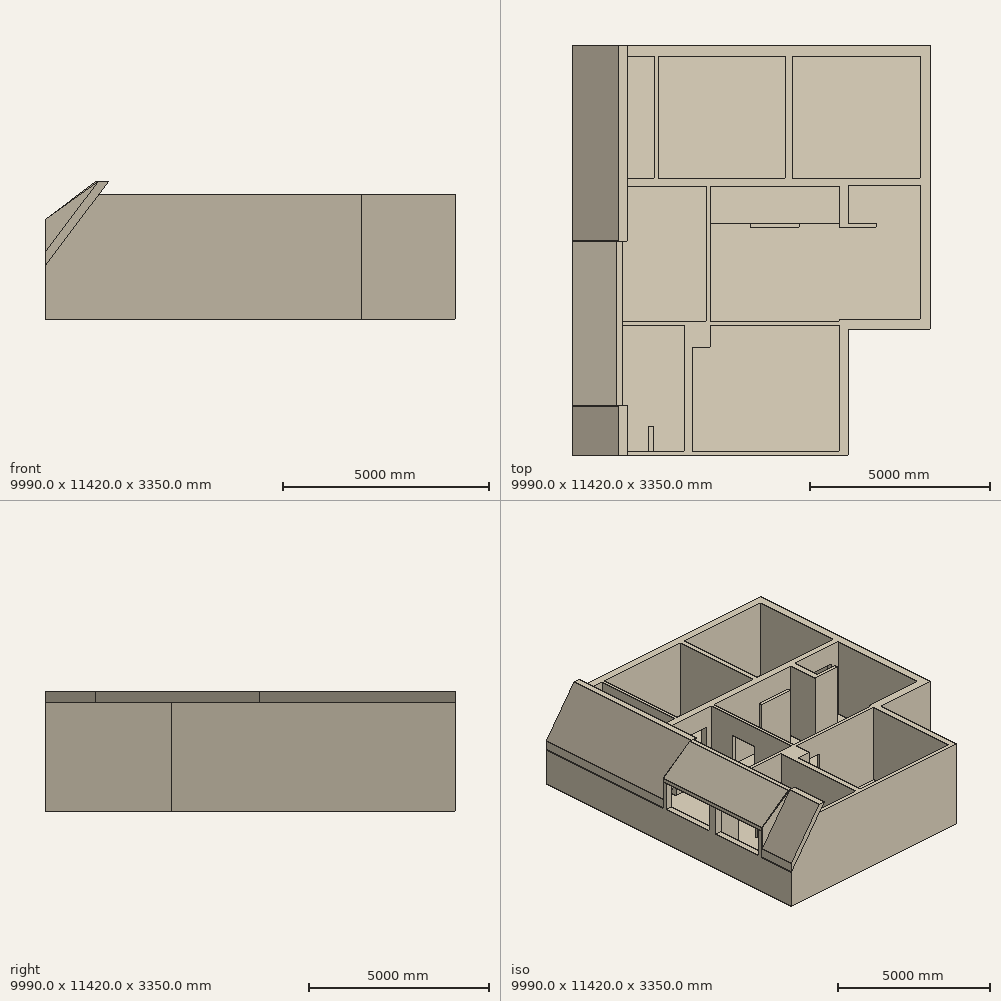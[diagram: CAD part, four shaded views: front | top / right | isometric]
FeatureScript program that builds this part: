
annotation { "Feature Type Name" : "Feature", "Feature Type Description" : "" }
export const myFeature = defineFeature(function(context is Context, id is Id, definition is map)
    precondition{}
    {
        {
            var Q0;
            Q0=qCreatedBy(makeId("Top.planeOp"),FACE);
            var sketch = newSketch(context, id + "F0", { "sketchPlane" : qUnion([Q0])});
            skLineSegment(sketch, "E0", {"start": v(0, 0) * mm, "end": v(0, 11420) * mm});
            skLineSegment(sketch, "E1", {"start": v(0, 11420) * mm, "end": v(9990, 11420) * mm});
            skLineSegment(sketch, "E2", {"start": v(0, 0) * mm, "end": v(7690, 0) * mm});
            skLineSegment(sketch, "E3", {"start": v(7690, 0) * mm, "end": v(7690, 3500) * mm});
            skLineSegment(sketch, "E4", {"start": v(7690, 3500) * mm, "end": v(9990, 3500) * mm});
            skLineSegment(sketch, "E5", {"start": v(9990, 3500) * mm, "end": v(9990, 11420) * mm});
            skSolve(sketch);
        }
        {
            var Q0;
            Q0 = qSketchRegion(id + "F0", true);
            extrude(context, id + "F1", {"entities" : qUnion([Q0]), "depth" : 300 * mm});
        }
        {
            var Q0;
            Q0=makeQuery(id+"F1.opExtrude","CAP_FACE",FACE,{"disambiguationData":[OSD([sQuery(id+"F0.wireOp",EDGE,"E0"),sQuery(id+"F0.wireOp",EDGE,"E1"),sQuery(id+"F0.wireOp",EDGE,"E2"),sQuery(id+"F0.wireOp",EDGE,"E3"),sQuery(id+"F0.wireOp",EDGE,"E4"),sQuery(id+"F0.wireOp",EDGE,"E5")])],"isStart":false});
            var sketch = newSketch(context, id + "F2", { "sketchPlane" : qUnion([Q0])});
            skLineSegment(sketch, "E6.bottom", {"start": v(0, 0) * mm, "end": v(7690, 0) * mm});
            skLineSegment(sketch, "E6.top", {"start": v(0, 120) * mm, "end": v(7690, 120) * mm});
            skLineSegment(sketch, "E6.left", {"start": v(0, 0) * mm, "end": v(0, 120) * mm});
            skLineSegment(sketch, "E6.right", {"start": v(7690, 0) * mm, "end": v(7690, 120) * mm});
            skSolve(sketch);
        }
        {
            var Q0;
            Q0 = qSketchRegion(id + "F2", true);
            extrude(context, id + "F3", {"entities" : qUnion([Q0]), "operationType" : NewBodyOperationType.ADD, "depth" : 2750 * mm});
        }
        {
            var Q0;
            Q0=makeQuery(id+"F1.opExtrude","CAP_FACE",FACE,{"disambiguationData":[OSD([sQuery(id+"F0.wireOp",EDGE,"E0"),sQuery(id+"F0.wireOp",EDGE,"E1"),sQuery(id+"F0.wireOp",EDGE,"E2"),sQuery(id+"F0.wireOp",EDGE,"E3"),sQuery(id+"F0.wireOp",EDGE,"E4"),sQuery(id+"F0.wireOp",EDGE,"E5")])],"isStart":false});
            var sketch = newSketch(context, id + "F4", { "sketchPlane" : qUnion([Q0])});
            skLineSegment(sketch, "E7.bottom", {"start": v(0, 120) * mm, "end": v(240, 120) * mm});
            skLineSegment(sketch, "E7.top", {"start": v(0, 7480) * mm, "end": v(240, 7480) * mm});
            skLineSegment(sketch, "E7.left", {"start": v(0, 120) * mm, "end": v(0, 7480) * mm});
            skLineSegment(sketch, "E7.right", {"start": v(240, 120) * mm, "end": v(240, 7480) * mm});
            skSolve(sketch);
        }
        {
            var Q0;
            Q0 = qSketchRegion(id + "F4", true);
            extrude(context, id + "F5", {"entities" : qUnion([Q0]), "operationType" : NewBodyOperationType.ADD, "depth" : 2750 * mm});
        }
        {
            var Q0;
            Q0=makeQuery(id+"F1.opExtrude","CAP_FACE",FACE,{"disambiguationData":[OSD([sQuery(id+"F0.wireOp",EDGE,"E0"),sQuery(id+"F0.wireOp",EDGE,"E1"),sQuery(id+"F0.wireOp",EDGE,"E2"),sQuery(id+"F0.wireOp",EDGE,"E3"),sQuery(id+"F0.wireOp",EDGE,"E4"),sQuery(id+"F0.wireOp",EDGE,"E5")])],"isStart":false});
            var sketch = newSketch(context, id + "F6", { "sketchPlane" : qUnion([Q0])});
            skLineSegment(sketch, "E8.bottom", {"start": v(7690, 120) * mm, "end": v(7450, 120) * mm});
            skLineSegment(sketch, "E8.left", {"start": v(7690, 120) * mm, "end": v(7690, 7480) * mm});
            skLineSegment(sketch, "E8.right", {"start": v(7450, 120) * mm, "end": v(7450, 7480) * mm});
            skLineSegment(sketch, "E9.bottom", {"start": v(0, 7480) * mm, "end": v(7450, 7480) * mm});
            skLineSegment(sketch, "E9.top", {"start": v(0, 7720) * mm, "end": v(7690, 7720) * mm});
            skLineSegment(sketch, "E9.left", {"start": v(0, 7480) * mm, "end": v(0, 7720) * mm});
            skLineSegment(sketch, "E9.right", {"start": v(7690, 7480) * mm, "end": v(7690, 7720) * mm});
            skSolve(sketch);
        }
        {
            var Q0;
            Q0 = qSketchRegion(id + "F6", true);
            extrude(context, id + "F7", {"entities" : qUnion([Q0]), "operationType" : NewBodyOperationType.ADD, "depth" : 2750 * mm});
        }
        {
            var Q0;
            {var subQ0=sQuery(id+"F0.wireOp",EDGE,"E5");var subQ1=sQuery(id+"F0.wireOp",EDGE,"E0");var subQ2=sQuery(id+"F0.wireOp",EDGE,"E3");var subQ3=sQuery(id+"F0.wireOp",EDGE,"E1");var subQ4=sQuery(id+"F0.wireOp",EDGE,"E4");Q0=makeQuery(id+"F7.boolean.opBoolean","SPLIT",FACE,{"disambiguationData":[TD([makeQuery(id+"F1.opExtrude","SWEPT_FACE",FACE,{"disambiguationData":[OSD([subQ1])]})])],"derivedFrom":makeQuery(id+"F1.opExtrude","CAP_FACE",FACE,{"disambiguationData":[OSD([subQ1,subQ3,sQuery(id+"F0.wireOp",EDGE,"E2"),subQ2,subQ4,subQ0])],"isStart":false})});}
            var sketch = newSketch(context, id + "F8", { "sketchPlane" : qUnion([Q0])});
            skLineSegment(sketch, "E10.top", {"start": v(0, 7720) * mm, "end": v(300, 7720) * mm});
            skLineSegment(sketch, "E10.left", {"start": v(0, 11420) * mm, "end": v(0, 7720) * mm});
            skLineSegment(sketch, "E11.top", {"start": v(9690, 11120) * mm, "end": v(300, 11120) * mm});
            skLineSegment(sketch, "E11.left", {"start": v(9990, 11420) * mm, "end": v(9990, 11120) * mm});
            skLineSegment(sketch, "E12.top", {"start": v(9990, 3500) * mm, "end": v(9690, 3500) * mm});
            skLineSegment(sketch, "E12.left", {"start": v(9990, 11420) * mm, "end": v(9990, 3500) * mm});
            skLineSegment(sketch, "E13", {"start": v(300, 7720) * mm, "end": v(300, 11120) * mm});
            skLineSegment(sketch, "E14", {"start": v(9690, 3800) * mm, "end": v(9690, 11120) * mm});
            skLineSegment(sketch, "E15.top", {"start": v(7690, 3800) * mm, "end": v(9690, 3800) * mm});
            skLineSegment(sketch, "E15.left", {"start": v(7690, 3500) * mm, "end": v(7690, 3800) * mm});
            skLineSegment(sketch, "E16", {"start": v(7690, 3500) * mm, "end": v(9690, 3500) * mm});
            skLineSegment(sketch, "E17", {"start": v(9990, 11420) * mm, "end": v(0, 11420) * mm});
            skSolve(sketch);
        }
        {
            var Q0;
            Q0=makeQuery(id+"F7.boolean.opBoolean","SPLIT",FACE,{"disambiguationData":[TD([makeQuery(id+"F3.opExtrude","SWEPT_FACE",FACE,{"disambiguationData":[OSD([sQuery(id+"F2.wireOp",EDGE,"E6.top")])]})])],"derivedFrom":makeQuery(id+"F1.opExtrude","CAP_FACE",FACE,{"disambiguationData":[OSD([sQuery(id+"F0.wireOp",EDGE,"E0"),sQuery(id+"F0.wireOp",EDGE,"E1"),sQuery(id+"F0.wireOp",EDGE,"E2"),sQuery(id+"F0.wireOp",EDGE,"E3"),sQuery(id+"F0.wireOp",EDGE,"E4"),sQuery(id+"F0.wireOp",EDGE,"E5")])],"isStart":false})});
            var sketch = newSketch(context, id + "F9", { "sketchPlane" : qUnion([Q0])});
            skLineSegment(sketch, "E18.bottom", {"start": v(240, 3730) * mm, "end": v(7450, 3730) * mm});
            skLineSegment(sketch, "E18.top", {"start": v(240, 3620) * mm, "end": v(7450, 3620) * mm});
            skLineSegment(sketch, "E18.left", {"start": v(240, 3730) * mm, "end": v(240, 3620) * mm});
            skLineSegment(sketch, "E18.right", {"start": v(7450, 3730) * mm, "end": v(7450, 3620) * mm});
            skSolve(sketch);
        }
        {
            var Q0;
            Q0 = qSketchRegion(id + "F9", true);
            extrude(context, id + "F10", {"entities" : qUnion([Q0]), "operationType" : NewBodyOperationType.ADD, "depth" : 2750 * mm});
        }
        {
            var Q0;
            Q0 = qSketchRegion(id + "F8", true);
            extrude(context, id + "F11", {"entities" : qUnion([Q0]), "operationType" : NewBodyOperationType.ADD, "depth" : 2750 * mm});
        }
        {
            var Q0;
            {var subQ0=makeQuery(id+"F3.opExtrude","SWEPT_FACE",FACE,{"disambiguationData":[OSD([sQuery(id+"F2.wireOp",EDGE,"E6.top")])]});Q0=makeQuery(id+"F10.boolean.opBoolean","SPLIT",FACE,{"disambiguationData":[TD([subQ0])],"derivedFrom":makeQuery(id+"F7.boolean.opBoolean","SPLIT",FACE,{"disambiguationData":[TD([subQ0])],"derivedFrom":makeQuery(id+"F1.opExtrude","CAP_FACE",FACE,{"disambiguationData":[OSD([sQuery(id+"F0.wireOp",EDGE,"E0"),sQuery(id+"F0.wireOp",EDGE,"E1"),sQuery(id+"F0.wireOp",EDGE,"E2"),sQuery(id+"F0.wireOp",EDGE,"E3"),sQuery(id+"F0.wireOp",EDGE,"E4"),sQuery(id+"F0.wireOp",EDGE,"E5")])],"isStart":false})})});}
            var sketch = newSketch(context, id + "F12", { "sketchPlane" : qUnion([Q0])});
            skLineSegment(sketch, "E19.bottom", {"start": v(3740, 120) * mm, "end": v(3850, 120) * mm});
            skLineSegment(sketch, "E19.top", {"start": v(3740, 3620) * mm, "end": v(3850, 3620) * mm});
            skLineSegment(sketch, "E19.left", {"start": v(3740, 120) * mm, "end": v(3740, 3620) * mm});
            skLineSegment(sketch, "E19.right", {"start": v(3850, 120) * mm, "end": v(3850, 3620) * mm});
            skSolve(sketch);
        }
        {
            var Q0;
            Q0 = qSketchRegion(id + "F12", true);
            extrude(context, id + "F13", {"entities" : qUnion([Q0]), "operationType" : NewBodyOperationType.ADD, "depth" : 2750 * mm});
        }
        {
            var Q0;
            {var subQ2=makeQuery(id+"F7.opExtrude","SWEPT_FACE",FACE,{"disambiguationData":[OSD([sQuery(id+"F6.wireOp",EDGE,"E9.bottom")])]});Q0=makeQuery(id+"F10.boolean.opBoolean","SPLIT",FACE,{"disambiguationData":[TD([subQ2])],"derivedFrom":makeQuery(id+"F7.boolean.opBoolean","SPLIT",FACE,{"disambiguationData":[TD([makeQuery(id+"F3.opExtrude","SWEPT_FACE",FACE,{"disambiguationData":[OSD([sQuery(id+"F2.wireOp",EDGE,"E6.top")])]})])],"derivedFrom":makeQuery(id+"F1.opExtrude","CAP_FACE",FACE,{"disambiguationData":[OSD([sQuery(id+"F0.wireOp",EDGE,"E0"),sQuery(id+"F0.wireOp",EDGE,"E1"),sQuery(id+"F0.wireOp",EDGE,"E2"),sQuery(id+"F0.wireOp",EDGE,"E3"),sQuery(id+"F0.wireOp",EDGE,"E4"),sQuery(id+"F0.wireOp",EDGE,"E5")])],"isStart":false})})});}
            var sketch = newSketch(context, id + "F14", { "sketchPlane" : qUnion([Q0])});
            skLineSegment(sketch, "E20.bottom", {"start": v(3740, 3730) * mm, "end": v(3850, 3730) * mm});
            skLineSegment(sketch, "E20.top", {"start": v(3740, 7480) * mm, "end": v(3850, 7480) * mm});
            skLineSegment(sketch, "E20.left", {"start": v(3740, 3730) * mm, "end": v(3740, 7480) * mm});
            skLineSegment(sketch, "E20.right", {"start": v(3850, 3730) * mm, "end": v(3850, 7480) * mm});
            skSolve(sketch);
        }
        {
            var Q0;
            Q0 = qSketchRegion(id + "F14", true);
            extrude(context, id + "F15", {"entities" : qUnion([Q0]), "operationType" : NewBodyOperationType.ADD, "depth" : 2750 * mm});
        }
        {
            var Q0;
            {var subQ0=sQuery(id+"F0.wireOp",EDGE,"E5");var subQ1=sQuery(id+"F0.wireOp",EDGE,"E0");var subQ2=sQuery(id+"F0.wireOp",EDGE,"E3");var subQ3=sQuery(id+"F0.wireOp",EDGE,"E1");var subQ4=sQuery(id+"F0.wireOp",EDGE,"E4");Q0=makeQuery(id+"F7.boolean.opBoolean","SPLIT",FACE,{"disambiguationData":[TD([makeQuery(id+"F1.opExtrude","SWEPT_FACE",FACE,{"disambiguationData":[OSD([subQ1])]})])],"derivedFrom":makeQuery(id+"F1.opExtrude","CAP_FACE",FACE,{"disambiguationData":[OSD([subQ1,subQ3,sQuery(id+"F0.wireOp",EDGE,"E2"),subQ2,subQ4,subQ0])],"isStart":false})});}
            var sketch = newSketch(context, id + "F16", { "sketchPlane" : qUnion([Q0])});
            skLineSegment(sketch, "E21.bottom", {"start": v(2300, 11120) * mm, "end": v(2410, 11120) * mm});
            skLineSegment(sketch, "E21.top", {"start": v(2300, 7720) * mm, "end": v(2410, 7720) * mm});
            skLineSegment(sketch, "E21.left", {"start": v(2300, 11120) * mm, "end": v(2300, 7720) * mm});
            skLineSegment(sketch, "E21.right", {"start": v(2410, 11120) * mm, "end": v(2410, 7720) * mm});
            skSolve(sketch);
        }
        {
            var Q0;
            Q0 = qSketchRegion(id + "F16", true);
            extrude(context, id + "F17", {"entities" : qUnion([Q0]), "operationType" : NewBodyOperationType.ADD, "depth" : 2750 * mm});
        }
        {
            var Q0;
            {var subQ3=sQuery(id+"F0.wireOp",EDGE,"E3");var subQ4=makeQuery(id+"F1.opExtrude","SWEPT_FACE",FACE,{"disambiguationData":[OSD([subQ3])]});var subQ5=sQuery(id+"F0.wireOp",EDGE,"E5");var subQ6=sQuery(id+"F0.wireOp",EDGE,"E0");var subQ7=sQuery(id+"F0.wireOp",EDGE,"E1");var subQ8=sQuery(id+"F0.wireOp",EDGE,"E4");Q0=makeQuery(id+"F17.boolean.opBoolean","SPLIT",FACE,{"disambiguationData":[TD([subQ4])],"derivedFrom":makeQuery(id+"F7.boolean.opBoolean","SPLIT",FACE,{"disambiguationData":[TD([makeQuery(id+"F1.opExtrude","SWEPT_FACE",FACE,{"disambiguationData":[OSD([subQ6])]})])],"derivedFrom":makeQuery(id+"F1.opExtrude","CAP_FACE",FACE,{"disambiguationData":[OSD([subQ6,subQ7,sQuery(id+"F0.wireOp",EDGE,"E2"),subQ3,subQ8,subQ5])],"isStart":false})})});}
            var sketch = newSketch(context, id + "F18", { "sketchPlane" : qUnion([Q0])});
            skLineSegment(sketch, "E22.bottom", {"start": v(7690, 7720) * mm, "end": v(9690, 7720) * mm});
            skLineSegment(sketch, "E22.top", {"start": v(7690, 7520) * mm, "end": v(9690, 7520) * mm});
            skLineSegment(sketch, "E22.left", {"start": v(7690, 7720) * mm, "end": v(7690, 7520) * mm});
            skLineSegment(sketch, "E22.right", {"start": v(9690, 7720) * mm, "end": v(9690, 7520) * mm});
            skSolve(sketch);
        }
        {
            var Q0;
            Q0 = qSketchRegion(id + "F18", true);
            extrude(context, id + "F19", {"entities" : qUnion([Q0]), "operationType" : NewBodyOperationType.ADD, "depth" : 2750 * mm});
        }
        {
            var Q0;
            {var subQ3=makeQuery(id+"F7.opExtrude","SWEPT_FACE",FACE,{"disambiguationData":[OSD([sQuery(id+"F6.wireOp",EDGE,"E9.top")])]});var subQ6=sQuery(id+"F0.wireOp",EDGE,"E3");var subQ7=makeQuery(id+"F1.opExtrude","SWEPT_FACE",FACE,{"disambiguationData":[OSD([subQ6])]});var subQ8=sQuery(id+"F0.wireOp",EDGE,"E5");var subQ9=sQuery(id+"F0.wireOp",EDGE,"E0");var subQ10=sQuery(id+"F0.wireOp",EDGE,"E1");var subQ11=sQuery(id+"F0.wireOp",EDGE,"E4");Q0=makeQuery(id+"F19.boolean.opBoolean","SPLIT",FACE,{"disambiguationData":[TD([subQ3])],"derivedFrom":makeQuery(id+"F17.boolean.opBoolean","SPLIT",FACE,{"disambiguationData":[TD([subQ7])],"derivedFrom":makeQuery(id+"F7.boolean.opBoolean","SPLIT",FACE,{"disambiguationData":[TD([makeQuery(id+"F1.opExtrude","SWEPT_FACE",FACE,{"disambiguationData":[OSD([subQ9])]})])],"derivedFrom":makeQuery(id+"F1.opExtrude","CAP_FACE",FACE,{"disambiguationData":[OSD([subQ9,subQ10,sQuery(id+"F0.wireOp",EDGE,"E2"),subQ6,subQ11,subQ8])],"isStart":false})})})});}
            var sketch = newSketch(context, id + "F20", { "sketchPlane" : qUnion([Q0])});
            skLineSegment(sketch, "E23.bottom", {"start": v(5950, 11120) * mm, "end": v(6150, 11120) * mm});
            skLineSegment(sketch, "E23.top", {"start": v(5950, 7720) * mm, "end": v(6150, 7720) * mm});
            skLineSegment(sketch, "E23.left", {"start": v(5950, 11120) * mm, "end": v(5950, 7720) * mm});
            skLineSegment(sketch, "E23.right", {"start": v(6150, 11120) * mm, "end": v(6150, 7720) * mm});
            skSolve(sketch);
        }
        {
            var Q0;
            Q0 = qSketchRegion(id + "F20", true);
            extrude(context, id + "F21", {"entities" : qUnion([Q0]), "operationType" : NewBodyOperationType.ADD, "depth" : 2750 * mm});
        }
        {
            var Q0;
            Q0=makeQuery(id+"F21.boolean.opBoolean","MERGE",FACE,{"derivedFrom":[makeQuery(id+"F19.boolean.opBoolean","MERGE",FACE,{"derivedFrom":[makeQuery(id+"F17.boolean.opBoolean","MERGE",FACE,{"derivedFrom":[makeQuery(id+"F15.boolean.opBoolean","MERGE",FACE,{"derivedFrom":[makeQuery(id+"F13.boolean.opBoolean","MERGE",FACE,{"derivedFrom":[makeQuery(id+"F11.boolean.opBoolean","MERGE",FACE,{"derivedFrom":[makeQuery(id+"F10.boolean.opBoolean","MERGE",FACE,{"derivedFrom":[makeQuery(id+"F7.boolean.opBoolean","MERGE",FACE,{"derivedFrom":[makeQuery(id+"F5.boolean.opBoolean","MERGE",FACE,{"derivedFrom":[makeQuery(id+"F3.opExtrude","CAP_FACE",FACE,{"disambiguationData":[OSD([sQuery(id+"F2.wireOp",EDGE,"E6.bottom"),sQuery(id+"F2.wireOp",EDGE,"E6.top"),sQuery(id+"F2.wireOp",EDGE,"E6.left"),sQuery(id+"F2.wireOp",EDGE,"E6.right")])],"isStart":false}),makeQuery(id+"F5.opExtrude","CAP_FACE",FACE,{"disambiguationData":[OSD([sQuery(id+"F4.wireOp",EDGE,"E7.bottom"),sQuery(id+"F4.wireOp",EDGE,"E7.top"),sQuery(id+"F4.wireOp",EDGE,"E7.left"),sQuery(id+"F4.wireOp",EDGE,"E7.right")])],"isStart":false})]}),makeQuery(id+"F7.opExtrude","CAP_FACE",FACE,{"disambiguationData":[OSD([sQuery(id+"F6.wireOp",EDGE,"E8.bottom"),sQuery(id+"F6.wireOp",EDGE,"E8.left"),sQuery(id+"F6.wireOp",EDGE,"E8.right"),sQuery(id+"F6.wireOp",EDGE,"E9.bottom"),sQuery(id+"F6.wireOp",EDGE,"E9.top"),sQuery(id+"F6.wireOp",EDGE,"E9.left"),sQuery(id+"F6.wireOp",EDGE,"E9.right")])],"isStart":false})]}),makeQuery(id+"F10.opExtrude","CAP_FACE",FACE,{"disambiguationData":[OSD([sQuery(id+"F9.wireOp",EDGE,"E18.bottom"),sQuery(id+"F9.wireOp",EDGE,"E18.top"),sQuery(id+"F9.wireOp",EDGE,"E18.left"),sQuery(id+"F9.wireOp",EDGE,"E18.right")])],"isStart":false})]}),makeQuery(id+"F11.opExtrude","CAP_FACE",FACE,{"disambiguationData":[OSD([sQuery(id+"F8.wireOp",EDGE,"E10.top"),sQuery(id+"F8.wireOp",EDGE,"E10.left"),sQuery(id+"F8.wireOp",EDGE,"E11.top"),sQuery(id+"F8.wireOp",EDGE,"E12.top"),sQuery(id+"F8.wireOp",EDGE,"E12.left"),sQuery(id+"F8.wireOp",EDGE,"E13"),sQuery(id+"F8.wireOp",EDGE,"E14"),sQuery(id+"F8.wireOp",EDGE,"E15.top"),sQuery(id+"F8.wireOp",EDGE,"E15.left"),sQuery(id+"F8.wireOp",EDGE,"E16"),sQuery(id+"F8.wireOp",EDGE,"E17")])],"isStart":false})]}),makeQuery(id+"F13.opExtrude","CAP_FACE",FACE,{"disambiguationData":[OSD([sQuery(id+"F12.wireOp",EDGE,"E19.bottom"),sQuery(id+"F12.wireOp",EDGE,"E19.top"),sQuery(id+"F12.wireOp",EDGE,"E19.left"),sQuery(id+"F12.wireOp",EDGE,"E19.right")])],"isStart":false})]}),makeQuery(id+"F15.opExtrude","CAP_FACE",FACE,{"disambiguationData":[OSD([sQuery(id+"F14.wireOp",EDGE,"E20.bottom"),sQuery(id+"F14.wireOp",EDGE,"E20.top"),sQuery(id+"F14.wireOp",EDGE,"E20.left"),sQuery(id+"F14.wireOp",EDGE,"E20.right")])],"isStart":false})]}),makeQuery(id+"F17.opExtrude","CAP_FACE",FACE,{"disambiguationData":[OSD([sQuery(id+"F16.wireOp",EDGE,"E21.bottom"),sQuery(id+"F16.wireOp",EDGE,"E21.top"),sQuery(id+"F16.wireOp",EDGE,"E21.left"),sQuery(id+"F16.wireOp",EDGE,"E21.right")])],"isStart":false})]}),makeQuery(id+"F19.opExtrude","CAP_FACE",FACE,{"disambiguationData":[OSD([sQuery(id+"F18.wireOp",EDGE,"E22.bottom"),sQuery(id+"F18.wireOp",EDGE,"E22.top"),sQuery(id+"F18.wireOp",EDGE,"E22.left"),sQuery(id+"F18.wireOp",EDGE,"E22.right")])],"isStart":false})]}),makeQuery(id+"F21.opExtrude","CAP_FACE",FACE,{"disambiguationData":[OSD([sQuery(id+"F20.wireOp",EDGE,"E23.bottom"),sQuery(id+"F20.wireOp",EDGE,"E23.top"),sQuery(id+"F20.wireOp",EDGE,"E23.left"),sQuery(id+"F20.wireOp",EDGE,"E23.right")])],"isStart":false})]});
            var sketch = newSketch(context, id + "F22", { "sketchPlane" : qUnion([Q0])});
            skLineSegment(sketch, "E24.bottom", {"start": v(7450, 6470) * mm, "end": v(7690, 6470) * mm});
            skLineSegment(sketch, "E24.top", {"start": v(7450, 3800) * mm, "end": v(7690, 3800) * mm});
            skLineSegment(sketch, "E24.left", {"start": v(7450, 6470) * mm, "end": v(7450, 3800) * mm});
            skLineSegment(sketch, "E24.right", {"start": v(7690, 6470) * mm, "end": v(7690, 3800) * mm});
            skSolve(sketch);
        }
        {
            var Q0;
            Q0 = qSketchRegion(id + "F22", true);
            extrude(context, id + "F23", {"entities" : qUnion([Q0]), "operationType" : NewBodyOperationType.REMOVE, "oppositeDirection" : true, "depth" : 2750 * mm});
        }
        {
            var Q0;
            {var subQ3=sQuery(id+"F0.wireOp",EDGE,"E3");var subQ4=makeQuery(id+"F1.opExtrude","SWEPT_FACE",FACE,{"disambiguationData":[OSD([subQ3])]});var subQ7=sQuery(id+"F0.wireOp",EDGE,"E5");var subQ8=sQuery(id+"F0.wireOp",EDGE,"E0");var subQ9=sQuery(id+"F0.wireOp",EDGE,"E1");var subQ10=sQuery(id+"F0.wireOp",EDGE,"E4");var subQ11=makeQuery(id+"F1.opExtrude","CAP_FACE",FACE,{"disambiguationData":[OSD([subQ8,subQ9,sQuery(id+"F0.wireOp",EDGE,"E2"),subQ3,subQ10,subQ7])],"isStart":false});var subQ12=makeQuery(id+"F7.opExtrude","SWEPT_FACE",FACE,{"disambiguationData":[OSD([sQuery(id+"F6.wireOp",EDGE,"E8.right")])]});var subQ13=makeQuery(id+"F7.opExtrude","SWEPT_FACE",FACE,{"disambiguationData":[OSD([sQuery(id+"F6.wireOp",EDGE,"E9.bottom")])]});Q0=makeQuery(id+"F23.boolean.opBoolean","MERGE",FACE,{"derivedFrom":[makeQuery(id+"F15.boolean.opBoolean","SPLIT",FACE,{"disambiguationData":[TD([subQ12])],"derivedFrom":makeQuery(id+"F10.boolean.opBoolean","SPLIT",FACE,{"disambiguationData":[TD([subQ13])],"derivedFrom":makeQuery(id+"F7.boolean.opBoolean","SPLIT",FACE,{"disambiguationData":[TD([makeQuery(id+"F3.opExtrude","SWEPT_FACE",FACE,{"disambiguationData":[OSD([sQuery(id+"F2.wireOp",EDGE,"E6.top")])]})])],"derivedFrom":subQ11})})}),makeQuery(id+"F19.boolean.opBoolean","SPLIT",FACE,{"disambiguationData":[TD([subQ4])],"derivedFrom":makeQuery(id+"F17.boolean.opBoolean","SPLIT",FACE,{"disambiguationData":[TD([subQ4])],"derivedFrom":makeQuery(id+"F7.boolean.opBoolean","SPLIT",FACE,{"disambiguationData":[TD([makeQuery(id+"F1.opExtrude","SWEPT_FACE",FACE,{"disambiguationData":[OSD([subQ8])]})])],"derivedFrom":subQ11})})}),makeQuery(id+"F23.opExtrude","CAP_FACE",FACE,{"disambiguationData":[OSD([sQuery(id+"F22.wireOp",EDGE,"E24.bottom"),sQuery(id+"F22.wireOp",EDGE,"E24.top"),sQuery(id+"F22.wireOp",EDGE,"E24.left"),sQuery(id+"F22.wireOp",EDGE,"E24.right")])],"isStart":false})]});}
            var sketch = newSketch(context, id + "F24", { "sketchPlane" : qUnion([Q0])});
            skLineSegment(sketch, "E25.bottom", {"start": v(7450, 7480) * mm, "end": v(3850, 7480) * mm});
            skLineSegment(sketch, "E25.top", {"start": v(7450, 6470) * mm, "end": v(3850, 6470) * mm});
            skLineSegment(sketch, "E25.left", {"start": v(7450, 7480) * mm, "end": v(7450, 6470) * mm});
            skLineSegment(sketch, "E25.right", {"start": v(3850, 7480) * mm, "end": v(3850, 6470) * mm});
            skSolve(sketch);
        }
        {
            var Q0;
            Q0 = qSketchRegion(id + "F24", true);
            extrude(context, id + "F25", {"entities" : qUnion([Q0]), "operationType" : NewBodyOperationType.ADD, "depth" : 100 * mm});
        }
        {
            var Q0;
            {var subQ0=makeQuery(id+"F3.opExtrude","SWEPT_FACE",FACE,{"disambiguationData":[OSD([sQuery(id+"F2.wireOp",EDGE,"E6.top")])]});var subQ1=makeQuery(id+"F5.opExtrude","SWEPT_FACE",FACE,{"disambiguationData":[OSD([sQuery(id+"F4.wireOp",EDGE,"E7.right")])]});Q0=makeQuery(id+"F13.boolean.opBoolean","SPLIT",FACE,{"disambiguationData":[TD([subQ1])],"derivedFrom":makeQuery(id+"F10.boolean.opBoolean","SPLIT",FACE,{"disambiguationData":[TD([subQ0])],"derivedFrom":makeQuery(id+"F7.boolean.opBoolean","SPLIT",FACE,{"disambiguationData":[TD([subQ0])],"derivedFrom":makeQuery(id+"F1.opExtrude","CAP_FACE",FACE,{"disambiguationData":[OSD([sQuery(id+"F0.wireOp",EDGE,"E0"),sQuery(id+"F0.wireOp",EDGE,"E1"),sQuery(id+"F0.wireOp",EDGE,"E2"),sQuery(id+"F0.wireOp",EDGE,"E3"),sQuery(id+"F0.wireOp",EDGE,"E4"),sQuery(id+"F0.wireOp",EDGE,"E5")])],"isStart":false})})})});}
            var sketch = newSketch(context, id + "F26", { "sketchPlane" : qUnion([Q0])});
            skLineSegment(sketch, "E26.bottom", {"start": v(3740, 3620) * mm, "end": v(3140, 3620) * mm});
            skLineSegment(sketch, "E26.top", {"start": v(3740, 3020) * mm, "end": v(3140, 3020) * mm});
            skLineSegment(sketch, "E26.left", {"start": v(3740, 3620) * mm, "end": v(3740, 3020) * mm});
            skLineSegment(sketch, "E26.right", {"start": v(3140, 3620) * mm, "end": v(3140, 3020) * mm});
            skSolve(sketch);
        }
        {
            var Q0;
            Q0 = qSketchRegion(id + "F26", true);
            extrude(context, id + "F27", {"entities" : qUnion([Q0]), "operationType" : NewBodyOperationType.ADD, "depth" : 2750 * mm});
        }
        {
            var Q0;
            {var subQ0=sQuery(id+"F4.wireOp",EDGE,"E7.right");var subQ2=sQuery(id+"F6.wireOp",EDGE,"E9.bottom");Q0=makeQuery(id+"F15.boolean.opBoolean","SPLIT",FACE,{"disambiguationData":[TD([makeQuery(id+"F5.opExtrude","SWEPT_FACE",FACE,{"disambiguationData":[OSD([subQ0])]})])],"derivedFrom":makeQuery(id+"F7.opExtrude","SWEPT_FACE",FACE,{"disambiguationData":[OSD([subQ2])]})});}
            var sketch = newSketch(context, id + "F28", { "sketchPlane" : qUnion([Q0])});
            skLineSegment(sketch, "E27.bottom", {"start": v(2627.5, 300) * mm, "end": v(3522.5, 300) * mm});
            skLineSegment(sketch, "E27.top", {"start": v(2627.5, 2320) * mm, "end": v(3522.5, 2320) * mm});
            skLineSegment(sketch, "E27.left", {"start": v(2627.5, 300) * mm, "end": v(2627.5, 2320) * mm});
            skLineSegment(sketch, "E27.right", {"start": v(3522.5, 300) * mm, "end": v(3522.5, 2320) * mm});
            skSolve(sketch);
        }
        {
            var Q0;
            Q0 = qSketchRegion(id + "F28", true);
            extrude(context, id + "F29", {"entities" : qUnion([Q0]), "operationType" : NewBodyOperationType.REMOVE, "oppositeDirection" : true, "depth" : 370 * mm});
        }
        {
            var Q0;
            Q0=makeQuery(id+"F19.opExtrude","SWEPT_FACE",FACE,{"disambiguationData":[OSD([sQuery(id+"F18.wireOp",EDGE,"E22.top")])]});
            var sketch = newSketch(context, id + "F30", { "sketchPlane" : qUnion([Q0])});
            skLineSegment(sketch, "E28.bottom", {"start": v(8495, 300) * mm, "end": v(9390, 300) * mm});
            skLineSegment(sketch, "E28.top", {"start": v(8495, 2320) * mm, "end": v(9390, 2320) * mm});
            skLineSegment(sketch, "E28.left", {"start": v(8495, 300) * mm, "end": v(8495, 2320) * mm});
            skLineSegment(sketch, "E28.right", {"start": v(9390, 300) * mm, "end": v(9390, 2320) * mm});
            skSolve(sketch);
        }
        {
            var Q0;
            Q0 = qSketchRegion(id + "F30", true);
            extrude(context, id + "F31", {"entities" : qUnion([Q0]), "operationType" : NewBodyOperationType.REMOVE, "oppositeDirection" : true, "depth" : 1000 * mm});
        }
        {
            var Q0;
            {var subQ0=sQuery(id+"F4.wireOp",EDGE,"E7.right");var subQ2=sQuery(id+"F6.wireOp",EDGE,"E9.bottom");Q0=makeQuery(id+"F15.boolean.opBoolean","SPLIT",FACE,{"disambiguationData":[TD([makeQuery(id+"F5.opExtrude","SWEPT_FACE",FACE,{"disambiguationData":[OSD([subQ0])]})])],"derivedFrom":makeQuery(id+"F7.opExtrude","SWEPT_FACE",FACE,{"disambiguationData":[OSD([subQ2])]})});}
            var sketch = newSketch(context, id + "F32", { "sketchPlane" : qUnion([Q0])});
            skLineSegment(sketch, "E29.bottom", {"start": v(1205, 300) * mm, "end": v(2100, 300) * mm});
            skLineSegment(sketch, "E29.top", {"start": v(1205, 2320) * mm, "end": v(2100, 2320) * mm});
            skLineSegment(sketch, "E29.left", {"start": v(1205, 300) * mm, "end": v(1205, 2320) * mm});
            skLineSegment(sketch, "E29.right", {"start": v(2100, 300) * mm, "end": v(2100, 2320) * mm});
            skSolve(sketch);
        }
        {
            var Q0;
            Q0 = qSketchRegion(id + "F32", true);
            extrude(context, id + "F33", {"entities" : qUnion([Q0]), "operationType" : NewBodyOperationType.REMOVE, "oppositeDirection" : true, "depth" : 700 * mm});
        }
        {
            var Q0;
            {var subQ0=sQuery(id+"F4.wireOp",EDGE,"E7.right");var subQ2=sQuery(id+"F9.wireOp",EDGE,"E18.top");Q0=makeQuery(id+"F13.boolean.opBoolean","SPLIT",FACE,{"disambiguationData":[TD([makeQuery(id+"F5.opExtrude","SWEPT_FACE",FACE,{"disambiguationData":[OSD([subQ0])]})])],"derivedFrom":makeQuery(id+"F10.opExtrude","SWEPT_FACE",FACE,{"disambiguationData":[OSD([subQ2])]})});}
            var sketch = newSketch(context, id + "F34", { "sketchPlane" : qUnion([Q0])});
            skLineSegment(sketch, "E30.bottom", {"start": v(2040, 300) * mm, "end": v(1145, 300) * mm});
            skLineSegment(sketch, "E30.top", {"start": v(2040, 2320) * mm, "end": v(1145, 2320) * mm});
            skLineSegment(sketch, "E30.left", {"start": v(2040, 300) * mm, "end": v(2040, 2320) * mm});
            skLineSegment(sketch, "E30.right", {"start": v(1145, 300) * mm, "end": v(1145, 2320) * mm});
            skSolve(sketch);
        }
        {
            var Q0;
            Q0 = qSketchRegion(id + "F34", true);
            extrude(context, id + "F35", {"entities" : qUnion([Q0]), "operationType" : NewBodyOperationType.REMOVE, "oppositeDirection" : true, "depth" : 390 * mm});
        }
        {
            var Q0;
            {var subQ0=sQuery(id+"F6.wireOp",EDGE,"E8.right");var subQ1=sQuery(id+"F9.wireOp",EDGE,"E18.top");Q0=makeQuery(id+"F13.boolean.opBoolean","SPLIT",FACE,{"disambiguationData":[TD([makeQuery(id+"F7.opExtrude","SWEPT_FACE",FACE,{"disambiguationData":[OSD([subQ0])]})])],"derivedFrom":makeQuery(id+"F10.opExtrude","SWEPT_FACE",FACE,{"disambiguationData":[OSD([subQ1])]})});}
            var sketch = newSketch(context, id + "F36", { "sketchPlane" : qUnion([Q0])});
            skLineSegment(sketch, "E31.bottom", {"start": v(4050, 300) * mm, "end": v(4945, 300) * mm});
            skLineSegment(sketch, "E31.top", {"start": v(4050, 2320) * mm, "end": v(4945, 2320) * mm});
            skLineSegment(sketch, "E31.left", {"start": v(4050, 300) * mm, "end": v(4050, 2320) * mm});
            skLineSegment(sketch, "E31.right", {"start": v(4945, 300) * mm, "end": v(4945, 2320) * mm});
            skSolve(sketch);
        }
        {
            var Q0;
            Q0 = qSketchRegion(id + "F36", true);
            extrude(context, id + "F37", {"entities" : qUnion([Q0]), "operationType" : NewBodyOperationType.REMOVE, "oppositeDirection" : true, "depth" : 360 * mm});
        }
        {
            var Q0;
            {var subQ0=makeQuery(id+"F11.opExtrude","SWEPT_FACE",FACE,{"disambiguationData":[OSD([sQuery(id+"F8.wireOp",EDGE,"E14")])]});var subQ3=sQuery(id+"F0.wireOp",EDGE,"E3");var subQ4=makeQuery(id+"F1.opExtrude","SWEPT_FACE",FACE,{"disambiguationData":[OSD([subQ3])]});var subQ6=makeQuery(id+"F7.opExtrude","SWEPT_FACE",FACE,{"disambiguationData":[OSD([sQuery(id+"F6.wireOp",EDGE,"E9.top")])]});var subQ9=sQuery(id+"F0.wireOp",EDGE,"E5");var subQ10=sQuery(id+"F0.wireOp",EDGE,"E0");var subQ11=sQuery(id+"F0.wireOp",EDGE,"E1");var subQ12=sQuery(id+"F0.wireOp",EDGE,"E4");var subQ13=makeQuery(id+"F1.opExtrude","CAP_FACE",FACE,{"disambiguationData":[OSD([subQ10,subQ11,sQuery(id+"F0.wireOp",EDGE,"E2"),subQ3,subQ12,subQ9])],"isStart":false});var subQ14=makeQuery(id+"F17.boolean.opBoolean","SPLIT",FACE,{"disambiguationData":[TD([subQ4])],"derivedFrom":makeQuery(id+"F7.boolean.opBoolean","SPLIT",FACE,{"disambiguationData":[TD([makeQuery(id+"F1.opExtrude","SWEPT_FACE",FACE,{"disambiguationData":[OSD([subQ10])]})])],"derivedFrom":subQ13})});var subQ15=makeQuery(id+"F7.opExtrude","SWEPT_FACE",FACE,{"disambiguationData":[OSD([sQuery(id+"F6.wireOp",EDGE,"E8.right")])]});var subQ16=makeQuery(id+"F7.opExtrude","SWEPT_FACE",FACE,{"disambiguationData":[OSD([sQuery(id+"F6.wireOp",EDGE,"E9.bottom")])]});var subQ19=makeQuery(id+"F3.opExtrude","SWEPT_FACE",FACE,{"disambiguationData":[OSD([sQuery(id+"F2.wireOp",EDGE,"E6.top")])]});var subQ20=makeQuery(id+"F7.boolean.opBoolean","SPLIT",FACE,{"disambiguationData":[TD([subQ19])],"derivedFrom":subQ13});Q0=makeQuery(id+"F37.boolean.opBoolean","MERGE",FACE,{"derivedFrom":[makeQuery(id+"F13.boolean.opBoolean","SPLIT",FACE,{"disambiguationData":[TD([subQ15])],"derivedFrom":makeQuery(id+"F10.boolean.opBoolean","SPLIT",FACE,{"disambiguationData":[TD([subQ19])],"derivedFrom":subQ20})}),makeQuery(id+"F31.boolean.opBoolean","MERGE",FACE,{"derivedFrom":[makeQuery(id+"F21.boolean.opBoolean","SPLIT",FACE,{"disambiguationData":[TD([subQ0])],"derivedFrom":makeQuery(id+"F19.boolean.opBoolean","SPLIT",FACE,{"disambiguationData":[TD([subQ6])],"derivedFrom":subQ14})}),makeQuery(id+"F23.boolean.opBoolean","MERGE",FACE,{"derivedFrom":[makeQuery(id+"F15.boolean.opBoolean","SPLIT",FACE,{"disambiguationData":[TD([subQ15])],"derivedFrom":makeQuery(id+"F10.boolean.opBoolean","SPLIT",FACE,{"disambiguationData":[TD([subQ16])],"derivedFrom":subQ20})}),makeQuery(id+"F19.boolean.opBoolean","SPLIT",FACE,{"disambiguationData":[TD([subQ4])],"derivedFrom":subQ14}),makeQuery(id+"F23.opExtrude","CAP_FACE",FACE,{"disambiguationData":[OSD([sQuery(id+"F22.wireOp",EDGE,"E24.bottom"),sQuery(id+"F22.wireOp",EDGE,"E24.top"),sQuery(id+"F22.wireOp",EDGE,"E24.left"),sQuery(id+"F22.wireOp",EDGE,"E24.right")])],"isStart":false})]}),makeQuery(id+"F31.opExtrude","SWEPT_FACE",FACE,{"disambiguationData":[OSD([sQuery(id+"F30.wireOp",EDGE,"E28.bottom")])]})]}),makeQuery(id+"F37.opExtrude","SWEPT_FACE",FACE,{"disambiguationData":[OSD([sQuery(id+"F36.wireOp",EDGE,"E31.bottom")])]})]});}
            var sketch = newSketch(context, id + "F38", { "sketchPlane" : qUnion([Q0])});
            skLineSegment(sketch, "E32.bottom", {"start": v(4970, 6470) * mm, "end": v(6320, 6470) * mm});
            skLineSegment(sketch, "E32.top", {"start": v(4970, 6350) * mm, "end": v(6320, 6350) * mm});
            skLineSegment(sketch, "E32.left", {"start": v(4970, 6470) * mm, "end": v(4970, 6350) * mm});
            skLineSegment(sketch, "E32.right", {"start": v(6320, 6470) * mm, "end": v(6320, 6350) * mm});
            skLineSegment(sketch, "E33.bottom", {"start": v(7450, 6470) * mm, "end": v(8490, 6470) * mm});
            skLineSegment(sketch, "E33.top", {"start": v(7450, 6350) * mm, "end": v(8490, 6350) * mm});
            skLineSegment(sketch, "E33.left", {"start": v(7450, 6470) * mm, "end": v(7450, 6350) * mm});
            skLineSegment(sketch, "E33.right", {"start": v(8490, 6470) * mm, "end": v(8490, 6350) * mm});
            skSolve(sketch);
        }
        {
            var Q0;
            Q0=makeQuery(id+"F15.opExtrude","SWEPT_FACE",FACE,{"disambiguationData":[OSD([sQuery(id+"F14.wireOp",EDGE,"E20.right")])]});
            var sketch = newSketch(context, id + "F39", { "sketchPlane" : qUnion([Q0])});
            skLineSegment(sketch, "E34.bottom", {"start": v(6470, 300) * mm, "end": v(5450, 300) * mm});
            skLineSegment(sketch, "E34.top", {"start": v(6470, 2320) * mm, "end": v(5450, 2320) * mm});
            skLineSegment(sketch, "E34.left", {"start": v(6470, 300) * mm, "end": v(6470, 2320) * mm});
            skLineSegment(sketch, "E34.right", {"start": v(5450, 300) * mm, "end": v(5450, 2320) * mm});
            skSolve(sketch);
        }
        {
            var Q0;
            Q0 = qSketchRegion(id + "F39", true);
            extrude(context, id + "F40", {"entities" : qUnion([Q0]), "operationType" : NewBodyOperationType.REMOVE, "oppositeDirection" : true, "depth" : 680 * mm});
        }
        {
            var Q0;
            {var subQ0=makeQuery(id+"F11.opExtrude","SWEPT_FACE",FACE,{"disambiguationData":[OSD([sQuery(id+"F8.wireOp",EDGE,"E14")])]});var subQ3=sQuery(id+"F0.wireOp",EDGE,"E3");var subQ4=makeQuery(id+"F1.opExtrude","SWEPT_FACE",FACE,{"disambiguationData":[OSD([subQ3])]});var subQ6=makeQuery(id+"F7.opExtrude","SWEPT_FACE",FACE,{"disambiguationData":[OSD([sQuery(id+"F6.wireOp",EDGE,"E9.top")])]});var subQ8=makeQuery(id+"F17.opExtrude","SWEPT_FACE",FACE,{"disambiguationData":[OSD([sQuery(id+"F16.wireOp",EDGE,"E21.right")])]});var subQ9=sQuery(id+"F0.wireOp",EDGE,"E5");var subQ10=sQuery(id+"F0.wireOp",EDGE,"E0");var subQ11=sQuery(id+"F0.wireOp",EDGE,"E1");var subQ12=sQuery(id+"F0.wireOp",EDGE,"E4");var subQ13=makeQuery(id+"F1.opExtrude","CAP_FACE",FACE,{"disambiguationData":[OSD([subQ10,subQ11,sQuery(id+"F0.wireOp",EDGE,"E2"),subQ3,subQ12,subQ9])],"isStart":false});var subQ14=makeQuery(id+"F7.boolean.opBoolean","SPLIT",FACE,{"disambiguationData":[TD([makeQuery(id+"F1.opExtrude","SWEPT_FACE",FACE,{"disambiguationData":[OSD([subQ10])]})])],"derivedFrom":subQ13});var subQ15=makeQuery(id+"F17.boolean.opBoolean","SPLIT",FACE,{"disambiguationData":[TD([subQ4])],"derivedFrom":subQ14});var subQ16=makeQuery(id+"F7.opExtrude","SWEPT_FACE",FACE,{"disambiguationData":[OSD([sQuery(id+"F6.wireOp",EDGE,"E8.right")])]});var subQ17=makeQuery(id+"F7.opExtrude","SWEPT_FACE",FACE,{"disambiguationData":[OSD([sQuery(id+"F6.wireOp",EDGE,"E9.bottom")])]});var subQ19=makeQuery(id+"F5.opExtrude","SWEPT_FACE",FACE,{"disambiguationData":[OSD([sQuery(id+"F4.wireOp",EDGE,"E7.right")])]});var subQ20=makeQuery(id+"F3.opExtrude","SWEPT_FACE",FACE,{"disambiguationData":[OSD([sQuery(id+"F2.wireOp",EDGE,"E6.top")])]});var subQ21=makeQuery(id+"F7.boolean.opBoolean","SPLIT",FACE,{"disambiguationData":[TD([subQ20])],"derivedFrom":subQ13});var subQ22=makeQuery(id+"F10.boolean.opBoolean","SPLIT",FACE,{"disambiguationData":[TD([subQ17])],"derivedFrom":subQ21});var subQ24=makeQuery(id+"F19.boolean.opBoolean","SPLIT",FACE,{"disambiguationData":[TD([subQ6])],"derivedFrom":subQ15});var subQ26=makeQuery(id+"F10.boolean.opBoolean","SPLIT",FACE,{"disambiguationData":[TD([subQ20])],"derivedFrom":subQ21});Q0=makeQuery(id+"F40.boolean.opBoolean","MERGE",FACE,{"derivedFrom":[makeQuery(id+"F35.boolean.opBoolean","MERGE",FACE,{"derivedFrom":[makeQuery(id+"F13.boolean.opBoolean","SPLIT",FACE,{"disambiguationData":[TD([subQ19])],"derivedFrom":subQ26}),makeQuery(id+"F33.boolean.opBoolean","MERGE",FACE,{"derivedFrom":[makeQuery(id+"F17.boolean.opBoolean","SPLIT",FACE,{"disambiguationData":[TD([makeQuery(id+"F11.opExtrude","SWEPT_FACE",FACE,{"disambiguationData":[OSD([sQuery(id+"F8.wireOp",EDGE,"E13")])]})])],"derivedFrom":subQ14}),makeQuery(id+"F29.boolean.opBoolean","MERGE",FACE,{"derivedFrom":[makeQuery(id+"F15.boolean.opBoolean","SPLIT",FACE,{"disambiguationData":[TD([subQ19])],"derivedFrom":subQ22}),makeQuery(id+"F21.boolean.opBoolean","SPLIT",FACE,{"disambiguationData":[TD([subQ8])],"derivedFrom":subQ24}),makeQuery(id+"F29.opExtrude","SWEPT_FACE",FACE,{"disambiguationData":[OSD([sQuery(id+"F28.wireOp",EDGE,"E27.bottom")])]})]}),makeQuery(id+"F33.opExtrude","SWEPT_FACE",FACE,{"disambiguationData":[OSD([sQuery(id+"F32.wireOp",EDGE,"E29.bottom")])]})]}),makeQuery(id+"F35.opExtrude","SWEPT_FACE",FACE,{"disambiguationData":[OSD([sQuery(id+"F34.wireOp",EDGE,"E30.bottom")])]})]}),makeQuery(id+"F37.boolean.opBoolean","MERGE",FACE,{"derivedFrom":[makeQuery(id+"F13.boolean.opBoolean","SPLIT",FACE,{"disambiguationData":[TD([subQ16])],"derivedFrom":subQ26}),makeQuery(id+"F31.boolean.opBoolean","MERGE",FACE,{"derivedFrom":[makeQuery(id+"F21.boolean.opBoolean","SPLIT",FACE,{"disambiguationData":[TD([subQ0])],"derivedFrom":subQ24}),makeQuery(id+"F23.boolean.opBoolean","MERGE",FACE,{"derivedFrom":[makeQuery(id+"F15.boolean.opBoolean","SPLIT",FACE,{"disambiguationData":[TD([subQ16])],"derivedFrom":subQ22}),makeQuery(id+"F19.boolean.opBoolean","SPLIT",FACE,{"disambiguationData":[TD([subQ4])],"derivedFrom":subQ15}),makeQuery(id+"F23.opExtrude","CAP_FACE",FACE,{"disambiguationData":[OSD([sQuery(id+"F22.wireOp",EDGE,"E24.bottom"),sQuery(id+"F22.wireOp",EDGE,"E24.top"),sQuery(id+"F22.wireOp",EDGE,"E24.left"),sQuery(id+"F22.wireOp",EDGE,"E24.right")])],"isStart":false})]}),makeQuery(id+"F31.opExtrude","SWEPT_FACE",FACE,{"disambiguationData":[OSD([sQuery(id+"F30.wireOp",EDGE,"E28.bottom")])]})]}),makeQuery(id+"F37.opExtrude","SWEPT_FACE",FACE,{"disambiguationData":[OSD([sQuery(id+"F36.wireOp",EDGE,"E31.bottom")])]})]}),makeQuery(id+"F40.opExtrude","SWEPT_FACE",FACE,{"disambiguationData":[OSD([sQuery(id+"F39.wireOp",EDGE,"E34.bottom")])]})]});}
            var sketch = newSketch(context, id + "F41", { "sketchPlane" : qUnion([Q0])});
            skLineSegment(sketch, "E35.bottom", {"start": v(3740, 120) * mm, "end": v(3850, 120) * mm});
            skLineSegment(sketch, "E35.top", {"start": v(3740, 3020) * mm, "end": v(3850, 3020) * mm});
            skLineSegment(sketch, "E35.left", {"start": v(3740, 120) * mm, "end": v(3740, 3020) * mm});
            skLineSegment(sketch, "E35.right", {"start": v(3850, 120) * mm, "end": v(3850, 3020) * mm});
            skSolve(sketch);
        }
        {
            var Q0;
            Q0 = qSketchRegion(id + "F41", true);
            extrude(context, id + "F42", {"entities" : qUnion([Q0]), "operationType" : NewBodyOperationType.REMOVE, "depth" : 3790 * mm});
        }
        {
            var Q0;
            Q0 = qSketchRegion(id + "F38", true);
            extrude(context, id + "F43", {"entities" : qUnion([Q0]), "operationType" : NewBodyOperationType.ADD, "depth" : 2750 * mm});
        }
        {
            var Q0;
            {var subQ0=makeQuery(id+"F11.opExtrude","SWEPT_FACE",FACE,{"disambiguationData":[OSD([sQuery(id+"F8.wireOp",EDGE,"E14")])]});var subQ3=sQuery(id+"F0.wireOp",EDGE,"E3");var subQ4=makeQuery(id+"F1.opExtrude","SWEPT_FACE",FACE,{"disambiguationData":[OSD([subQ3])]});var subQ6=makeQuery(id+"F7.opExtrude","SWEPT_FACE",FACE,{"disambiguationData":[OSD([sQuery(id+"F6.wireOp",EDGE,"E9.top")])]});var subQ8=makeQuery(id+"F17.opExtrude","SWEPT_FACE",FACE,{"disambiguationData":[OSD([sQuery(id+"F16.wireOp",EDGE,"E21.right")])]});var subQ9=sQuery(id+"F0.wireOp",EDGE,"E5");var subQ10=sQuery(id+"F0.wireOp",EDGE,"E0");var subQ11=sQuery(id+"F0.wireOp",EDGE,"E1");var subQ12=sQuery(id+"F0.wireOp",EDGE,"E4");var subQ13=makeQuery(id+"F1.opExtrude","CAP_FACE",FACE,{"disambiguationData":[OSD([subQ10,subQ11,sQuery(id+"F0.wireOp",EDGE,"E2"),subQ3,subQ12,subQ9])],"isStart":false});var subQ14=makeQuery(id+"F7.boolean.opBoolean","SPLIT",FACE,{"disambiguationData":[TD([makeQuery(id+"F1.opExtrude","SWEPT_FACE",FACE,{"disambiguationData":[OSD([subQ10])]})])],"derivedFrom":subQ13});var subQ15=makeQuery(id+"F17.boolean.opBoolean","SPLIT",FACE,{"disambiguationData":[TD([subQ4])],"derivedFrom":subQ14});var subQ16=makeQuery(id+"F7.opExtrude","SWEPT_FACE",FACE,{"disambiguationData":[OSD([sQuery(id+"F6.wireOp",EDGE,"E8.right")])]});var subQ17=makeQuery(id+"F7.opExtrude","SWEPT_FACE",FACE,{"disambiguationData":[OSD([sQuery(id+"F6.wireOp",EDGE,"E9.bottom")])]});var subQ19=makeQuery(id+"F5.opExtrude","SWEPT_FACE",FACE,{"disambiguationData":[OSD([sQuery(id+"F4.wireOp",EDGE,"E7.right")])]});var subQ20=makeQuery(id+"F3.opExtrude","SWEPT_FACE",FACE,{"disambiguationData":[OSD([sQuery(id+"F2.wireOp",EDGE,"E6.top")])]});var subQ21=makeQuery(id+"F7.boolean.opBoolean","SPLIT",FACE,{"disambiguationData":[TD([subQ20])],"derivedFrom":subQ13});var subQ22=makeQuery(id+"F10.boolean.opBoolean","SPLIT",FACE,{"disambiguationData":[TD([subQ17])],"derivedFrom":subQ21});var subQ24=makeQuery(id+"F19.boolean.opBoolean","SPLIT",FACE,{"disambiguationData":[TD([subQ6])],"derivedFrom":subQ15});var subQ26=makeQuery(id+"F10.boolean.opBoolean","SPLIT",FACE,{"disambiguationData":[TD([subQ20])],"derivedFrom":subQ21});Q0=makeQuery(id+"F42.boolean.opBoolean","MERGE",FACE,{"derivedFrom":[makeQuery(id+"F40.boolean.opBoolean","MERGE",FACE,{"derivedFrom":[makeQuery(id+"F35.boolean.opBoolean","MERGE",FACE,{"derivedFrom":[makeQuery(id+"F13.boolean.opBoolean","SPLIT",FACE,{"disambiguationData":[TD([subQ19])],"derivedFrom":subQ26}),makeQuery(id+"F33.boolean.opBoolean","MERGE",FACE,{"derivedFrom":[makeQuery(id+"F17.boolean.opBoolean","SPLIT",FACE,{"disambiguationData":[TD([makeQuery(id+"F11.opExtrude","SWEPT_FACE",FACE,{"disambiguationData":[OSD([sQuery(id+"F8.wireOp",EDGE,"E13")])]})])],"derivedFrom":subQ14}),makeQuery(id+"F29.boolean.opBoolean","MERGE",FACE,{"derivedFrom":[makeQuery(id+"F15.boolean.opBoolean","SPLIT",FACE,{"disambiguationData":[TD([subQ19])],"derivedFrom":subQ22}),makeQuery(id+"F21.boolean.opBoolean","SPLIT",FACE,{"disambiguationData":[TD([subQ8])],"derivedFrom":subQ24}),makeQuery(id+"F29.opExtrude","SWEPT_FACE",FACE,{"disambiguationData":[OSD([sQuery(id+"F28.wireOp",EDGE,"E27.bottom")])]})]}),makeQuery(id+"F33.opExtrude","SWEPT_FACE",FACE,{"disambiguationData":[OSD([sQuery(id+"F32.wireOp",EDGE,"E29.bottom")])]})]}),makeQuery(id+"F35.opExtrude","SWEPT_FACE",FACE,{"disambiguationData":[OSD([sQuery(id+"F34.wireOp",EDGE,"E30.bottom")])]})]}),makeQuery(id+"F37.boolean.opBoolean","MERGE",FACE,{"derivedFrom":[makeQuery(id+"F13.boolean.opBoolean","SPLIT",FACE,{"disambiguationData":[TD([subQ16])],"derivedFrom":subQ26}),makeQuery(id+"F31.boolean.opBoolean","MERGE",FACE,{"derivedFrom":[makeQuery(id+"F21.boolean.opBoolean","SPLIT",FACE,{"disambiguationData":[TD([subQ0])],"derivedFrom":subQ24}),makeQuery(id+"F23.boolean.opBoolean","MERGE",FACE,{"derivedFrom":[makeQuery(id+"F15.boolean.opBoolean","SPLIT",FACE,{"disambiguationData":[TD([subQ16])],"derivedFrom":subQ22}),makeQuery(id+"F19.boolean.opBoolean","SPLIT",FACE,{"disambiguationData":[TD([subQ4])],"derivedFrom":subQ15}),makeQuery(id+"F23.opExtrude","CAP_FACE",FACE,{"disambiguationData":[OSD([sQuery(id+"F22.wireOp",EDGE,"E24.bottom"),sQuery(id+"F22.wireOp",EDGE,"E24.top"),sQuery(id+"F22.wireOp",EDGE,"E24.left"),sQuery(id+"F22.wireOp",EDGE,"E24.right")])],"isStart":false})]}),makeQuery(id+"F31.opExtrude","SWEPT_FACE",FACE,{"disambiguationData":[OSD([sQuery(id+"F30.wireOp",EDGE,"E28.bottom")])]})]}),makeQuery(id+"F37.opExtrude","SWEPT_FACE",FACE,{"disambiguationData":[OSD([sQuery(id+"F36.wireOp",EDGE,"E31.bottom")])]})]}),makeQuery(id+"F40.opExtrude","SWEPT_FACE",FACE,{"disambiguationData":[OSD([sQuery(id+"F39.wireOp",EDGE,"E34.bottom")])]})]}),makeQuery(id+"F42.opExtrude","CAP_FACE",FACE,{"disambiguationData":[OSD([sQuery(id+"F41.wireOp",EDGE,"E35.bottom"),sQuery(id+"F41.wireOp",EDGE,"E35.top"),sQuery(id+"F41.wireOp",EDGE,"E35.left"),sQuery(id+"F41.wireOp",EDGE,"E35.right")])],"isStart":true})]});}
            var sketch = newSketch(context, id + "F44", { "sketchPlane" : qUnion([Q0])});
            skLineSegment(sketch, "E36.bottom", {"start": v(3140, 3020) * mm, "end": v(3340, 3020) * mm});
            skLineSegment(sketch, "E36.top", {"start": v(3140, 120) * mm, "end": v(3340, 120) * mm});
            skLineSegment(sketch, "E36.left", {"start": v(3140, 3020) * mm, "end": v(3140, 120) * mm});
            skLineSegment(sketch, "E36.right", {"start": v(3340, 3020) * mm, "end": v(3340, 120) * mm});
            skSolve(sketch);
        }
        {
            var Q0;
            Q0 = qSketchRegion(id + "F44", true);
            extrude(context, id + "F45", {"entities" : qUnion([Q0]), "operationType" : NewBodyOperationType.ADD, "depth" : 2750 * mm});
        }
        {
            var Q0;
            Q0=makeQuery(id+"F3.boolean.opBoolean","MERGE",FACE,{"derivedFrom":[makeQuery(id+"F1.opExtrude","SWEPT_FACE",FACE,{"disambiguationData":[OSD([sQuery(id+"F0.wireOp",EDGE,"E2")])]}),makeQuery(id+"F3.opExtrude","SWEPT_FACE",FACE,{"disambiguationData":[OSD([sQuery(id+"F2.wireOp",EDGE,"E6.bottom")])]})]});
            var sketch = newSketch(context, id + "F46", { "sketchPlane" : qUnion([Q0])});
            skLineSegment(sketch, "E37", {"start": v(0, 1300) * mm, "end": v(3795, 6350) * mm});
            skLineSegment(sketch, "E38", {"start": v(3795, 6350) * mm, "end": v(0, 6350) * mm});
            skLineSegment(sketch, "E39", {"start": v(0, 6350) * mm, "end": v(0, 1300) * mm});
            skSolve(sketch);
        }
        {
            var Q0;
            Q0 = qSketchRegion(id + "F46", true);
            extrude(context, id + "F47", {"entities" : qUnion([Q0]), "operationType" : NewBodyOperationType.REMOVE, "oppositeDirection" : true, "depth" : 1380 * mm});
        }
        {
            var Q0;
            Q0=makeQuery(id+"F11.boolean.opBoolean","MERGE",FACE,{"derivedFrom":[makeQuery(id+"F1.opExtrude","SWEPT_FACE",FACE,{"disambiguationData":[OSD([sQuery(id+"F0.wireOp",EDGE,"E1")])]}),makeQuery(id+"F11.opExtrude","SWEPT_FACE",FACE,{"disambiguationData":[OSD([sQuery(id+"F8.wireOp",EDGE,"E17")])]})]});
            var sketch = newSketch(context, id + "F48", { "sketchPlane" : qUnion([Q0])});
            skLineSegment(sketch, "E40", {"start": v(0, 1300) * mm, "end": v(-2132.04, 4137.1) * mm});
            skLineSegment(sketch, "E41", {"start": v(-2132.04, 4137.1) * mm, "end": v(0, 4137.1) * mm});
            skLineSegment(sketch, "E42", {"start": v(0, 4137.1) * mm, "end": v(0, 1300) * mm});
            skSolve(sketch);
        }
        {
            var Q0;
            Q0 = qSketchRegion(id + "F48", true);
            extrude(context, id + "F49", {"entities" : qUnion([Q0]), "operationType" : NewBodyOperationType.REMOVE, "oppositeDirection" : true, "depth" : 5460 * mm});
        }
        {
            var Q0;
            Q0=makeQuery(id+"F47.boolean.opBoolean","COPY",FACE,{"derivedFrom":makeQuery(id+"F47.opExtrude","CAP_FACE",FACE,{"disambiguationData":[OSD([sQuery(id+"F46.wireOp",EDGE,"E37"),sQuery(id+"F46.wireOp",EDGE,"E38"),sQuery(id+"F46.wireOp",EDGE,"E39")])],"isStart":false})});
            var sketch = newSketch(context, id + "F50", { "sketchPlane" : qUnion([Q0])});
            skLineSegment(sketch, "E43", {"start": v(0, 2300) * mm, "end": v(0, 5050) * mm});
            skLineSegment(sketch, "E44", {"start": v(0, 5050) * mm, "end": v(3649.37, 5050) * mm});
            skLineSegment(sketch, "E45", {"start": v(3649.37, 5050) * mm, "end": v(0, 2300) * mm});
            skSolve(sketch);
        }
        {
            var Q0;
            Q0 = qSketchRegion(id + "F50", true);
            extrude(context, id + "F51", {"entities" : qUnion([Q0]), "operationType" : NewBodyOperationType.REMOVE, "oppositeDirection" : true, "depth" : 5090 * mm});
        }
        {
            var Q0;
            Q0=makeQuery(id+"F3.boolean.opBoolean","MERGE",FACE,{"derivedFrom":[makeQuery(id+"F1.opExtrude","SWEPT_FACE",FACE,{"disambiguationData":[OSD([sQuery(id+"F0.wireOp",EDGE,"E2")])]}),makeQuery(id+"F3.opExtrude","SWEPT_FACE",FACE,{"disambiguationData":[OSD([sQuery(id+"F2.wireOp",EDGE,"E6.bottom")])]})]});
            var sketch = newSketch(context, id + "F52", { "sketchPlane" : qUnion([Q0])});
            skLineSegment(sketch, "E46", {"start": v(0, 1300) * mm, "end": v(1540.54, 3350) * mm});
            skLineSegment(sketch, "E47", {"start": v(0, 1300) * mm, "end": v(0, 1632.91) * mm});
            skLineSegment(sketch, "E48", {"start": v(0, 1632.91) * mm, "end": v(1290.37, 3350) * mm});
            skLineSegment(sketch, "E49", {"start": v(1290.37, 3350) * mm, "end": v(1540.54, 3350) * mm});
            skSolve(sketch);
        }
        {
            var Q0;
            Q0 = qSketchRegion(id + "F52", true);
            var Q1;
            Q1=makeQuery(id+"F47.boolean.opBoolean","COPY",FACE,{"derivedFrom":makeQuery(id+"F47.opExtrude","CAP_FACE",FACE,{"disambiguationData":[OSD([sQuery(id+"F46.wireOp",EDGE,"E37"),sQuery(id+"F46.wireOp",EDGE,"E38"),sQuery(id+"F46.wireOp",EDGE,"E39")])],"isStart":false})});
            extrude(context, id + "F53", {"entities" : qUnion([Q0]), "endBound" : BoundingType.UP_TO_SURFACE, "oppositeDirection" : true, "endBoundEntityFace" : qUnion([Q1]), "depth" : 25 * mm});
        }
        {
            var Q0;
            Q0=makeQuery(id+"F11.boolean.opBoolean","MERGE",FACE,{"derivedFrom":[makeQuery(id+"F1.opExtrude","SWEPT_FACE",FACE,{"disambiguationData":[OSD([sQuery(id+"F0.wireOp",EDGE,"E1")])]}),makeQuery(id+"F11.opExtrude","SWEPT_FACE",FACE,{"disambiguationData":[OSD([sQuery(id+"F8.wireOp",EDGE,"E17")])]})]});
            var sketch = newSketch(context, id + "F54", { "sketchPlane" : qUnion([Q0])});
            skLineSegment(sketch, "E50", {"start": v(0, 1300) * mm, "end": v(-1540.54, 3350) * mm});
            skLineSegment(sketch, "E51", {"start": v(-1540.54, 3350) * mm, "end": v(-1290.37, 3350) * mm});
            skLineSegment(sketch, "E52", {"start": v(-1290.37, 3350) * mm, "end": v(0, 1632.91) * mm});
            skLineSegment(sketch, "E53", {"start": v(0, 1300) * mm, "end": v(0, 1632.91) * mm});
            skSolve(sketch);
        }
        {
            var Q0;
            Q0 = qSketchRegion(id + "F54", true);
            extrude(context, id + "F55", {"entities" : qUnion([Q0]), "oppositeDirection" : true, "depth" : 5460 * mm});
        }
        {
            var Q0;
            Q0=makeQuery(id+"F47.boolean.opBoolean","COPY",FACE,{"derivedFrom":makeQuery(id+"F47.opExtrude","CAP_FACE",FACE,{"disambiguationData":[OSD([sQuery(id+"F46.wireOp",EDGE,"E37"),sQuery(id+"F46.wireOp",EDGE,"E38"),sQuery(id+"F46.wireOp",EDGE,"E39")])],"isStart":false})});
            var sketch = newSketch(context, id + "F56", { "sketchPlane" : qUnion([Q0])});
            skLineSegment(sketch, "E54", {"start": v(0, 2300) * mm, "end": v(1393.4, 3350) * mm});
            skLineSegment(sketch, "E55", {"start": v(0, 2300) * mm, "end": v(0, 2425.21) * mm});
            skLineSegment(sketch, "E56", {"start": v(0, 2425.21) * mm, "end": v(1227.23, 3350) * mm});
            skLineSegment(sketch, "E57", {"start": v(1393.4, 3350) * mm, "end": v(1227.23, 3350) * mm});
            skPoint(sketch, "E58.orphan", {"position": v(1393.4, 3475.21) * mm});
            skSolve(sketch);
        }
        {
            var Q0;
            Q0 = qSketchRegion(id + "F56", true);
            var Q1;
            Q1=makeQuery(id+"F55.opExtrude","CAP_FACE",FACE,{"disambiguationData":[OSD([sQuery(id+"F54.wireOp",EDGE,"E50"),sQuery(id+"F54.wireOp",EDGE,"E51"),sQuery(id+"F54.wireOp",EDGE,"E52"),sQuery(id+"F54.wireOp",EDGE,"E53")])],"isStart":false});
            extrude(context, id + "F57", {"entities" : qUnion([Q0]), "endBound" : BoundingType.UP_TO_SURFACE, "oppositeDirection" : true, "endBoundEntityFace" : qUnion([Q1]), "depth" : 2290 * mm});
        }
        {
            var Q0;
            Q0=makeQuery(id+"F47.boolean.opBoolean","COPY",FACE,{"derivedFrom":makeQuery(id+"F47.opExtrude","CAP_FACE",FACE,{"disambiguationData":[OSD([sQuery(id+"F46.wireOp",EDGE,"E37"),sQuery(id+"F46.wireOp",EDGE,"E38"),sQuery(id+"F46.wireOp",EDGE,"E39")])],"isStart":false})});
            var sketch = newSketch(context, id + "F58", { "sketchPlane" : qUnion([Q0])});
            skLineSegment(sketch, "E59", {"start": v(0, 2425.21) * mm, "end": v(1290.37, 3350) * mm});
            skLineSegment(sketch, "E60", {"start": v(1290.37, 3350) * mm, "end": v(0, 1632.91) * mm});
            skLineSegment(sketch, "E61", {"start": v(0, 2425.21) * mm, "end": v(0, 1632.91) * mm});
            skSolve(sketch);
        }
        {
            var Q0;
            Q0=makeQuery(id+"F49.boolean.opBoolean","COPY",FACE,{"derivedFrom":makeQuery(id+"F49.opExtrude","CAP_FACE",FACE,{"disambiguationData":[OSD([sQuery(id+"F48.wireOp",EDGE,"E40"),sQuery(id+"F48.wireOp",EDGE,"E41"),sQuery(id+"F48.wireOp",EDGE,"E42")])],"isStart":false})});
            var sketch = newSketch(context, id + "F59", { "sketchPlane" : qUnion([Q0])});
            skLineSegment(sketch, "E62", {"start": v(0, 1632.91) * mm, "end": v(-1290.37, 3350) * mm});
            skLineSegment(sketch, "E63", {"start": v(-1290.37, 3350) * mm, "end": v(0, 2425.21) * mm});
            skLineSegment(sketch, "E64", {"start": v(0, 2425.21) * mm, "end": v(0, 1632.91) * mm});
            skSolve(sketch);
        }
        {
            var Q0;
            Q0 = qSketchRegion(id + "F59", true);
            extrude(context, id + "F60", {"entities" : qUnion([Q0]), "depth" : 25 * mm});
        }
        {
            var Q0;
            Q0=makeQuery(id+"F11.boolean.opBoolean","MERGE",FACE,{"derivedFrom":[makeQuery(id+"F7.boolean.opBoolean","MERGE",FACE,{"derivedFrom":[makeQuery(id+"F5.boolean.opBoolean","MERGE",FACE,{"derivedFrom":[makeQuery(id+"F3.boolean.opBoolean","MERGE",FACE,{"derivedFrom":[makeQuery(id+"F1.opExtrude","SWEPT_FACE",FACE,{"disambiguationData":[OSD([sQuery(id+"F0.wireOp",EDGE,"E0")])]}),makeQuery(id+"F3.opExtrude","SWEPT_FACE",FACE,{"disambiguationData":[OSD([sQuery(id+"F2.wireOp",EDGE,"E6.left")])]})]}),makeQuery(id+"F5.opExtrude","SWEPT_FACE",FACE,{"disambiguationData":[OSD([sQuery(id+"F4.wireOp",EDGE,"E7.left")])]})]}),makeQuery(id+"F7.opExtrude","SWEPT_FACE",FACE,{"disambiguationData":[OSD([sQuery(id+"F6.wireOp",EDGE,"E9.left")])]})]}),makeQuery(id+"F11.opExtrude","SWEPT_FACE",FACE,{"disambiguationData":[OSD([sQuery(id+"F8.wireOp",EDGE,"E10.left")])]})]});
            var sketch = newSketch(context, id + "F61", { "sketchPlane" : qUnion([Q0])});
            skLineSegment(sketch, "E65.bottom", {"start": v(-5830, 2300) * mm, "end": v(-3830, 2300) * mm});
            skLineSegment(sketch, "E65.top", {"start": v(-5830, 1300) * mm, "end": v(-3830, 1300) * mm});
            skLineSegment(sketch, "E65.left", {"start": v(-5830, 2300) * mm, "end": v(-5830, 1300) * mm});
            skLineSegment(sketch, "E65.right", {"start": v(-3830, 2300) * mm, "end": v(-3830, 1300) * mm});
            skLineSegment(sketch, "E66.bottom", {"start": v(-3520, 2300) * mm, "end": v(-1520, 2300) * mm});
            skLineSegment(sketch, "E66.top", {"start": v(-3520, 1300) * mm, "end": v(-1520, 1300) * mm});
            skLineSegment(sketch, "E66.left", {"start": v(-3520, 2300) * mm, "end": v(-3520, 1300) * mm});
            skLineSegment(sketch, "E66.right", {"start": v(-1520, 2300) * mm, "end": v(-1520, 1300) * mm});
            skSolve(sketch);
        }
        {
            var Q0;
            Q0 = qSketchRegion(id + "F61", true);
            extrude(context, id + "F62", {"entities" : qUnion([Q0]), "operationType" : NewBodyOperationType.REMOVE, "oppositeDirection" : true, "depth" : 1310 * mm});
        }
        {
            var Q0;
            Q0 = qSketchRegion(id + "F58", true);
            extrude(context, id + "F63", {"entities" : qUnion([Q0]), "depth" : 25 * mm});
        }
        {
            var Q0;
            {var subQ0=makeQuery(id+"F11.opExtrude","SWEPT_FACE",FACE,{"disambiguationData":[OSD([sQuery(id+"F8.wireOp",EDGE,"E14")])]});var subQ3=sQuery(id+"F0.wireOp",EDGE,"E3");var subQ4=makeQuery(id+"F1.opExtrude","SWEPT_FACE",FACE,{"disambiguationData":[OSD([subQ3])]});var subQ6=makeQuery(id+"F7.opExtrude","SWEPT_FACE",FACE,{"disambiguationData":[OSD([sQuery(id+"F6.wireOp",EDGE,"E9.top")])]});var subQ8=makeQuery(id+"F17.opExtrude","SWEPT_FACE",FACE,{"disambiguationData":[OSD([sQuery(id+"F16.wireOp",EDGE,"E21.right")])]});var subQ9=sQuery(id+"F0.wireOp",EDGE,"E5");var subQ10=sQuery(id+"F0.wireOp",EDGE,"E0");var subQ11=sQuery(id+"F0.wireOp",EDGE,"E1");var subQ12=sQuery(id+"F0.wireOp",EDGE,"E4");var subQ13=makeQuery(id+"F1.opExtrude","CAP_FACE",FACE,{"disambiguationData":[OSD([subQ10,subQ11,sQuery(id+"F0.wireOp",EDGE,"E2"),subQ3,subQ12,subQ9])],"isStart":false});var subQ14=makeQuery(id+"F7.boolean.opBoolean","SPLIT",FACE,{"disambiguationData":[TD([makeQuery(id+"F1.opExtrude","SWEPT_FACE",FACE,{"disambiguationData":[OSD([subQ10])]})])],"derivedFrom":subQ13});var subQ15=makeQuery(id+"F17.boolean.opBoolean","SPLIT",FACE,{"disambiguationData":[TD([subQ4])],"derivedFrom":subQ14});var subQ16=makeQuery(id+"F7.opExtrude","SWEPT_FACE",FACE,{"disambiguationData":[OSD([sQuery(id+"F6.wireOp",EDGE,"E8.right")])]});var subQ17=makeQuery(id+"F7.opExtrude","SWEPT_FACE",FACE,{"disambiguationData":[OSD([sQuery(id+"F6.wireOp",EDGE,"E9.bottom")])]});var subQ19=makeQuery(id+"F5.opExtrude","SWEPT_FACE",FACE,{"disambiguationData":[OSD([sQuery(id+"F4.wireOp",EDGE,"E7.right")])]});var subQ20=makeQuery(id+"F3.opExtrude","SWEPT_FACE",FACE,{"disambiguationData":[OSD([sQuery(id+"F2.wireOp",EDGE,"E6.top")])]});var subQ21=makeQuery(id+"F7.boolean.opBoolean","SPLIT",FACE,{"disambiguationData":[TD([subQ20])],"derivedFrom":subQ13});var subQ22=makeQuery(id+"F10.boolean.opBoolean","SPLIT",FACE,{"disambiguationData":[TD([subQ17])],"derivedFrom":subQ21});var subQ24=makeQuery(id+"F19.boolean.opBoolean","SPLIT",FACE,{"disambiguationData":[TD([subQ6])],"derivedFrom":subQ15});var subQ26=makeQuery(id+"F10.boolean.opBoolean","SPLIT",FACE,{"disambiguationData":[TD([subQ20])],"derivedFrom":subQ21});Q0=makeQuery(id+"F42.boolean.opBoolean","MERGE",FACE,{"derivedFrom":[makeQuery(id+"F40.boolean.opBoolean","MERGE",FACE,{"derivedFrom":[makeQuery(id+"F35.boolean.opBoolean","MERGE",FACE,{"derivedFrom":[makeQuery(id+"F13.boolean.opBoolean","SPLIT",FACE,{"disambiguationData":[TD([subQ19])],"derivedFrom":subQ26}),makeQuery(id+"F33.boolean.opBoolean","MERGE",FACE,{"derivedFrom":[makeQuery(id+"F17.boolean.opBoolean","SPLIT",FACE,{"disambiguationData":[TD([makeQuery(id+"F11.opExtrude","SWEPT_FACE",FACE,{"disambiguationData":[OSD([sQuery(id+"F8.wireOp",EDGE,"E13")])]})])],"derivedFrom":subQ14}),makeQuery(id+"F29.boolean.opBoolean","MERGE",FACE,{"derivedFrom":[makeQuery(id+"F15.boolean.opBoolean","SPLIT",FACE,{"disambiguationData":[TD([subQ19])],"derivedFrom":subQ22}),makeQuery(id+"F21.boolean.opBoolean","SPLIT",FACE,{"disambiguationData":[TD([subQ8])],"derivedFrom":subQ24}),makeQuery(id+"F29.opExtrude","SWEPT_FACE",FACE,{"disambiguationData":[OSD([sQuery(id+"F28.wireOp",EDGE,"E27.bottom")])]})]}),makeQuery(id+"F33.opExtrude","SWEPT_FACE",FACE,{"disambiguationData":[OSD([sQuery(id+"F32.wireOp",EDGE,"E29.bottom")])]})]}),makeQuery(id+"F35.opExtrude","SWEPT_FACE",FACE,{"disambiguationData":[OSD([sQuery(id+"F34.wireOp",EDGE,"E30.bottom")])]})]}),makeQuery(id+"F37.boolean.opBoolean","MERGE",FACE,{"derivedFrom":[makeQuery(id+"F13.boolean.opBoolean","SPLIT",FACE,{"disambiguationData":[TD([subQ16])],"derivedFrom":subQ26}),makeQuery(id+"F31.boolean.opBoolean","MERGE",FACE,{"derivedFrom":[makeQuery(id+"F21.boolean.opBoolean","SPLIT",FACE,{"disambiguationData":[TD([subQ0])],"derivedFrom":subQ24}),makeQuery(id+"F23.boolean.opBoolean","MERGE",FACE,{"derivedFrom":[makeQuery(id+"F15.boolean.opBoolean","SPLIT",FACE,{"disambiguationData":[TD([subQ16])],"derivedFrom":subQ22}),makeQuery(id+"F19.boolean.opBoolean","SPLIT",FACE,{"disambiguationData":[TD([subQ4])],"derivedFrom":subQ15}),makeQuery(id+"F23.opExtrude","CAP_FACE",FACE,{"disambiguationData":[OSD([sQuery(id+"F22.wireOp",EDGE,"E24.bottom"),sQuery(id+"F22.wireOp",EDGE,"E24.top"),sQuery(id+"F22.wireOp",EDGE,"E24.left"),sQuery(id+"F22.wireOp",EDGE,"E24.right")])],"isStart":false})]}),makeQuery(id+"F31.opExtrude","SWEPT_FACE",FACE,{"disambiguationData":[OSD([sQuery(id+"F30.wireOp",EDGE,"E28.bottom")])]})]}),makeQuery(id+"F37.opExtrude","SWEPT_FACE",FACE,{"disambiguationData":[OSD([sQuery(id+"F36.wireOp",EDGE,"E31.bottom")])]})]}),makeQuery(id+"F40.opExtrude","SWEPT_FACE",FACE,{"disambiguationData":[OSD([sQuery(id+"F39.wireOp",EDGE,"E34.bottom")])]})]}),makeQuery(id+"F42.opExtrude","CAP_FACE",FACE,{"disambiguationData":[OSD([sQuery(id+"F41.wireOp",EDGE,"E35.bottom"),sQuery(id+"F41.wireOp",EDGE,"E35.top"),sQuery(id+"F41.wireOp",EDGE,"E35.left"),sQuery(id+"F41.wireOp",EDGE,"E35.right")])],"isStart":true})]});}
            var sketch = newSketch(context, id + "F64", { "sketchPlane" : qUnion([Q0])});
            skLineSegment(sketch, "E67.bottom", {"start": v(2260, 120) * mm, "end": v(2140, 120) * mm});
            skLineSegment(sketch, "E67.top", {"start": v(2260, 820) * mm, "end": v(2140, 820) * mm});
            skLineSegment(sketch, "E67.left", {"start": v(2260, 120) * mm, "end": v(2260, 820) * mm});
            skLineSegment(sketch, "E67.right", {"start": v(2140, 120) * mm, "end": v(2140, 820) * mm});
            skSolve(sketch);
        }
        {
            var Q0;
            Q0 = qSketchRegion(id + "F64", true);
            extrude(context, id + "F65", {"entities" : qUnion([Q0]), "operationType" : NewBodyOperationType.ADD, "depth" : 555 * mm});
        }
    });
